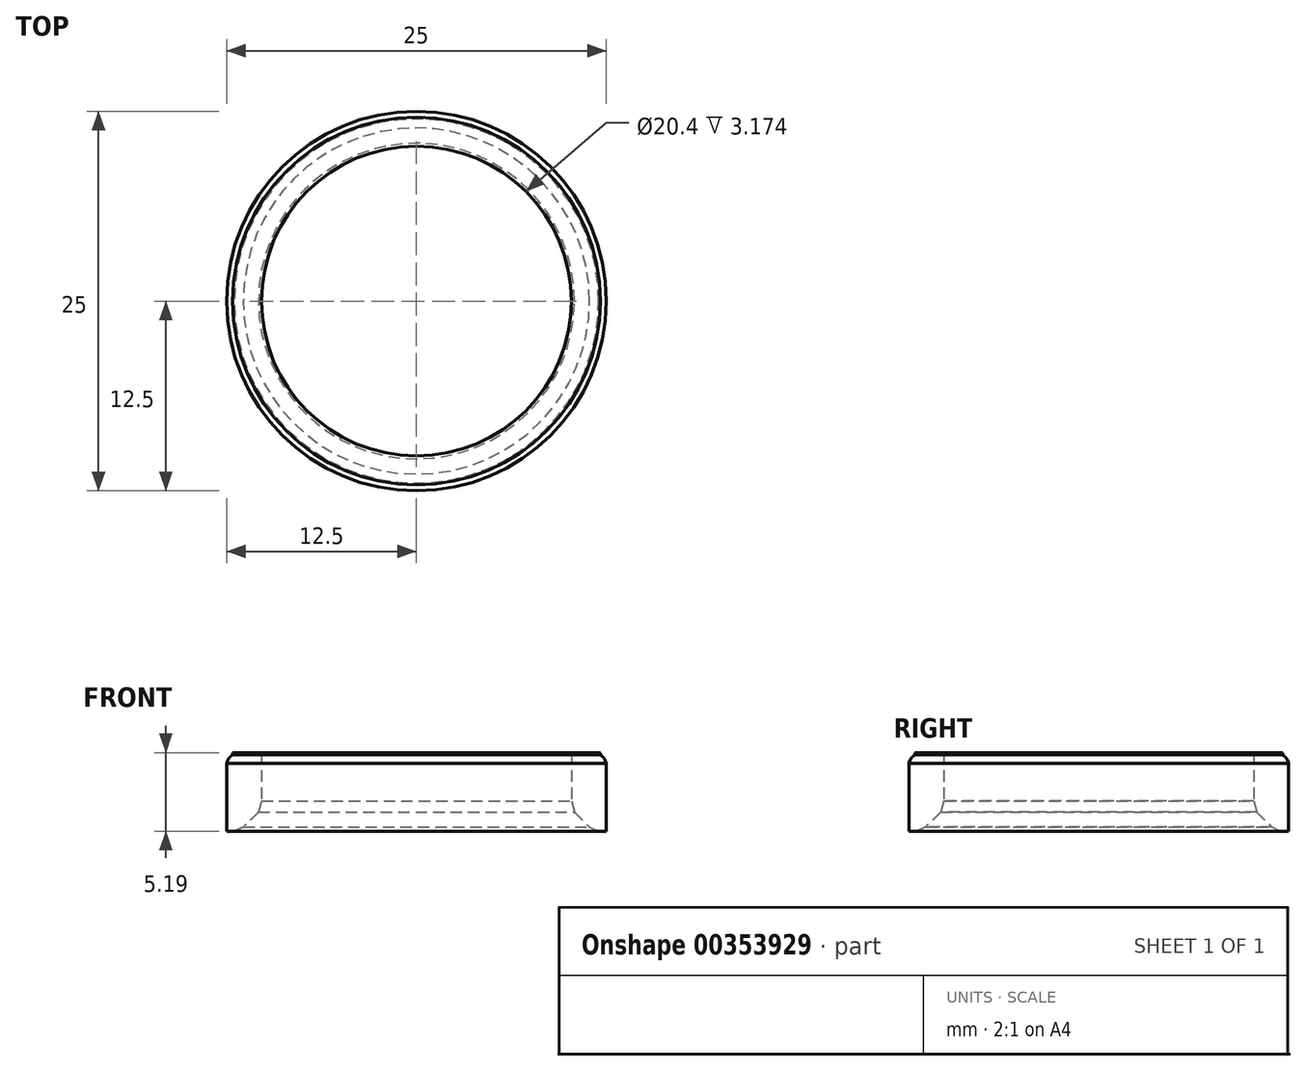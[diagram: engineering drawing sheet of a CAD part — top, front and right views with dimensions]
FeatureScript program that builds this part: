
annotation { "Feature Type Name" : "Feature", "Feature Type Description" : "" }
export const myFeature = defineFeature(function(context is Context, id is Id, definition is map)
    precondition{}
    {
        {
            var Q0;
            Q0=qCreatedBy(makeId("Front.planeOp"),FACE);
            var sketch = newSketch(context, id + "F0", { "sketchPlane" : qUnion([Q0])});
            skLineSegment(sketch, "E0", {"start": v(0, -5.16) * mm, "end": v(0, 98.57) * mm, "construction": true});
            skLineSegment(sketch, "E1", {"start": v(11.55, 1.17) * mm, "end": v(9.58, 3.1) * mm});
            skLineSegment(sketch, "E2", {"start": v(9.05, 3.1) * mm, "end": v(7.54, 3.65) * mm});
            skLineSegment(sketch, "E3", {"start": v(11.55, 1.17) * mm, "end": v(11.55, 0.45) * mm});
            skLineSegment(sketch, "E4", {"start": v(11.55, 0.45) * mm, "end": v(11.1, 0) * mm});
            skLineSegment(sketch, "E5", {"start": v(11.1, 0) * mm, "end": v(0, 0) * mm});
            skLineSegment(sketch, "E6", {"start": v(0, 98.57) * mm, "end": v(0, 0) * mm});
            skArc(sketch, "E7", {"start": v(2.94, 9.86) * mm, "mid": v(4.3, 6.06) * mm, "end": v(7.54, 3.65) * mm});
            skLineSegment(sketch, "E8", {"start": v(10.2, 6.22) * mm, "end": v(10.2, 3.04) * mm});
            skLineSegment(sketch, "E9", {"start": v(10.2, 3.04) * mm, "end": v(10.4, 2.3) * mm});
            skLineSegment(sketch, "E10", {"start": v(10.4, 2.3) * mm, "end": v(11.4, 1.31) * mm});
            skLineSegment(sketch, "E11", {"start": v(12, 1.03) * mm, "end": v(11.4, 1.31) * mm});
            skLineSegment(sketch, "E12", {"start": v(12.11, 6.22) * mm, "end": v(10.2, 6.22) * mm});
            skLineSegment(sketch, "E13", {"start": v(12, 1.03) * mm, "end": v(12.5, 1.03) * mm});
            skLineSegment(sketch, "E14", {"start": v(12.5, 1.03) * mm, "end": v(12.5, 5.52) * mm});
            skArc(sketch, "E15", {"start": v(12.45, 5.66) * mm, "mid": v(12.32, 5.89) * mm, "end": v(12.11, 6.07) * mm});
            skLineSegment(sketch, "E16", {"start": v(12.11, 6.07) * mm, "end": v(12.11, 6.22) * mm});
            skLineSegment(sketch, "E17", {"start": v(12.5, 5.52) * mm, "end": v(12.45, 5.66) * mm});
            skLineSegment(sketch, "E18", {"start": v(9.58, 3.1) * mm, "end": v(9.05, 3.1) * mm});
            skLineSegment(sketch, "E19", {"start": v(2.94, 9.86) * mm, "end": v(2.7, 14.52) * mm});
            skLineSegment(sketch, "E20", {"start": v(2.5, 16.86) * mm, "end": v(2.5, 98.57) * mm});
            skArc(sketch, "E21", {"start": v(2.5, 16.86) * mm, "mid": v(2.55, 15.69) * mm, "end": v(2.7, 14.52) * mm});
            skLineSegment(sketch, "E22", {"start": v(2.5, 98.57) * mm, "end": v(0, 98.57) * mm});
            skSolve(sketch);
        }
        {
            var Q0;
            Q0=makeQuery(id+"F0.imprint","IMPRINT",FACE,{"disambiguationData":[TD([[makeQuery(id+"F0.imprint","IMPRINT",EDGE,{"derivedFrom":sQuery(id+"F0.wireOp",EDGE,"E8")}),1.0]])]});
            var Q1;
            Q1=sQuery(id+"F0.wireOp",EDGE,"E0");
            revolve(context, id + "F1", {"surfaceOperationType" : NewSurfaceOperationType.NEW, "entities" : qUnion([Q0]), "axis" : qUnion([Q1]), "revolveType" : RevolveType.FULL});
        }
    });
